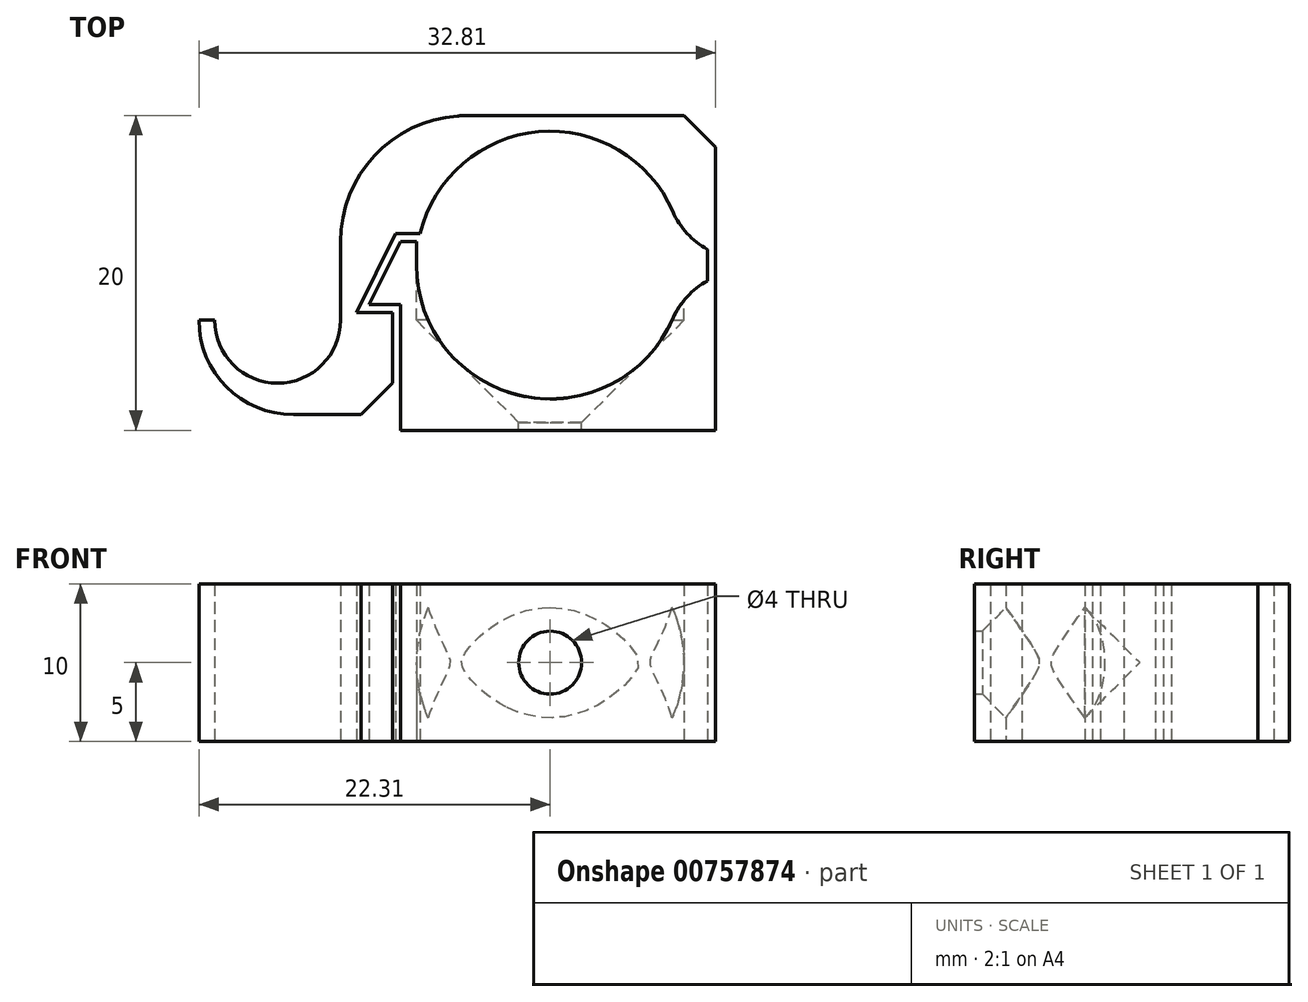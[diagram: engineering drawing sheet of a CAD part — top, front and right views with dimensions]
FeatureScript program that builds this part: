
annotation { "Feature Type Name" : "Feature", "Feature Type Description" : "" }
export const myFeature = defineFeature(function(context is Context, id is Id, definition is map)
    precondition{}
    {
        {
            var Q0;
            Q0=qCreatedBy(makeId("Top.planeOp"),FACE);
            var sketch = newSketch(context, id + "F0", { "sketchPlane" : qUnion([Q0])});
            skArc(sketch, "E0", {"start": v(-8.5, 0) * mm, "mid": v(8.44, -1) * mm, "end": v(-8.26, 2) * mm});
            skLineSegment(sketch, "E1", {"start": v(-9.5, 1.5) * mm, "end": v(-11.5, -2.5) * mm});
            skLineSegment(sketch, "E2", {"start": v(-11.5, -2.5) * mm, "end": v(-9.5, -2.5) * mm});
            skLineSegment(sketch, "E3", {"start": v(-9.5, -2.5) * mm, "end": v(-9.5, -10.5) * mm});
            skLineSegment(sketch, "E4", {"start": v(-9.5, -10.5) * mm, "end": v(10.5, -10.5) * mm});
            skLineSegment(sketch, "E5", {"start": v(10.5, -10.5) * mm, "end": v(10.5, 10.5) * mm});
            skCircle(sketch, "E6.0", {"center": v(0, 0) * mm, "radius": 10.5 * mm, "construction": true});
            skLineSegment(sketch, "E7", {"start": v(10.5, 10.5) * mm, "end": v(-13.3, 10.5) * mm});
            skLineSegment(sketch, "E8", {"start": v(-9.5, 1.5) * mm, "end": v(-8.5, 1.5) * mm});
            skLineSegment(sketch, "E9", {"start": v(-13.3, 10.5) * mm, "end": v(-13.3, -3.5) * mm});
            skLineSegment(sketch, "E10", {"start": v(-8.5, 1.5) * mm, "end": v(-8.5, 0) * mm});
            skLineSegment(sketch, "E11.0", {"start": v(-9.8, 2) * mm, "end": v(-8.26, 2) * mm});
            skLineSegment(sketch, "E11.1", {"start": v(-9.8, 2) * mm, "end": v(-12.3, -3) * mm});
            skLineSegment(sketch, "E12.0", {"start": v(-12.3, -3) * mm, "end": v(-10, -3) * mm});
            skLineSegment(sketch, "E13", {"start": v(-10, -3) * mm, "end": v(-10, -9.5) * mm});
            skLineSegment(sketch, "E14", {"start": v(-10, -9.5) * mm, "end": v(-13.3, -9.5) * mm});
            skLineSegment(sketch, "E15", {"start": v(-13.3, -9.5) * mm, "end": v(-22.3, -9.5) * mm});
            skLineSegment(sketch, "E16", {"start": v(-22.3, -9.5) * mm, "end": v(-22.3, -3.5) * mm});
            skLineSegment(sketch, "E17", {"start": v(-22.3, -3.5) * mm, "end": v(-21.3, -3.5) * mm});
            skArc(sketch, "E18", {"start": v(-21.3, -3.5) * mm, "mid": v(-17.3, -7.5) * mm, "end": v(-13.3, -3.5) * mm});
            skPoint(sketch, "E19", {"position": v(-17.3, -7.5) * mm});
            skPoint(sketch, "E20", {"position": v(8.5, 0) * mm});
            skLineSegment(sketch, "E21.bottom", {"start": v(7, 1) * mm, "end": v(10, 1) * mm});
            skLineSegment(sketch, "E21.top", {"start": v(7, -1) * mm, "end": v(10, -1) * mm});
            skLineSegment(sketch, "E21.left", {"start": v(7, 1) * mm, "end": v(7, -1) * mm});
            skLineSegment(sketch, "E21.right", {"start": v(10, 1) * mm, "end": v(10, -1) * mm});
            skLineSegment(sketch, "E22", {"start": v(-13.3, 9.5) * mm, "end": v(10.5, 9.5) * mm});
            skPoint(sketch, "E23", {"position": v(0, 8.5) * mm});
            skSolve(sketch);
        }
        {
            var Q0;
            Q0=makeQuery(id+"F0.imprint","IMPRINT",FACE,{"disambiguationData":[TD([[makeQuery(id+"F0.imprint","IMPRINT",EDGE,{"derivedFrom":sQuery(id+"F0.wireOp",EDGE,"E1")}),1.0]])]});
            extrude(context, id + "F1", {"entities" : qUnion([Q0]), "endBound" : BoundingType.SYMMETRIC, "depth" : 10 * mm, "offsetDistance" : 25 * mm});
        }
        {
            var Q0;
            Q0=qCreatedBy(makeId("Top.planeOp"),FACE);
            var sketch = newSketch(context, id + "F2", { "sketchPlane" : qUnion([Q0])});
            skLineSegment(sketch, "E24", {"start": v(0, 0) * mm, "end": v(0, -10.5) * mm, "construction": true});
            skPoint(sketch, "E25", {"position": v(-8.5, 1.5) * mm});
            skLineSegment(sketch, "E26", {"start": v(-8.5, 1.5) * mm, "end": v(-8.5, -3.5) * mm});
            skLineSegment(sketch, "E27", {"start": v(-8.5, -3.5) * mm, "end": v(-2, -10) * mm});
            skLineSegment(sketch, "E28", {"start": v(-2, -10) * mm, "end": v(-2, -10.5) * mm});
            skLineSegment(sketch, "E29", {"start": v(-2, -10.5) * mm, "end": v(0, -10.5) * mm});
            skLineSegment(sketch, "E30", {"start": v(-8.5, 1.5) * mm, "end": v(0, 1.5) * mm});
            skLineSegment(sketch, "E31", {"start": v(0, 1.5) * mm, "end": v(0, -10.5) * mm});
            skLineSegment(sketch, "E32", {"start": v(0.13, 0) * mm, "end": v(-8.5, 0) * mm});
            skSolve(sketch);
        }
        {
            var Q0;
            {var subQ1=sQuery(id+"F2.wireOp",EDGE,"E27");Q0=makeQuery(id+"F2.imprint","IMPRINT",FACE,{"disambiguationData":[TD([[makeQuery(id+"F2.imprint","IMPRINT",EDGE,{"derivedFrom":subQ1}),1.0]])]});}
            var Q1;
            Q1=sQuery(id+"F2.wireOp",EDGE,"E31");
            revolve(context, id + "F3", {"operationType" : NewBodyOperationType.REMOVE, "surfaceOperationType" : NewSurfaceOperationType.NEW, "entities" : qUnion([Q0]), "axis" : qUnion([Q1]), "revolveType" : RevolveType.FULL});
        }
        {
            var Q0;
            Q0=makeQuery(id+"F1.opExtrude","SWEPT_EDGE",EDGE,{"disambiguationData":[OSD([sQuery(id+"F0.wireOp",EDGE,"E13"),sQuery(id+"F0.wireOp",EDGE,"E14")])]});
            chamfer(context, id + "F4", {"entities" : qUnion([Q0]), "width" : 2 * mm, "tangentPropagation" : true});
        }
        {
            var Q0;
            Q0=makeQuery(id+"F1.opExtrude","SWEPT_EDGE",EDGE,{"disambiguationData":[OSD([sQuery(id+"F0.wireOp",EDGE,"E15"),sQuery(id+"F0.wireOp",EDGE,"E16")])]});
            fillet(context, id + "F5", {"entities" : qUnion([Q0]), "radius" : 6 * mm, "tangentPropagation" : true, "allowEdgeOverflow" : false});
        }
        {
            var Q0;
            Q0=makeQuery(id+"F1.opExtrude","SWEPT_EDGE",EDGE,{"disambiguationData":[OSD([sQuery(id+"F0.wireOp",EDGE,"E7"),sQuery(id+"F0.wireOp",EDGE,"E9")])]});
            chamfer(context, id + "F6", {"entities" : qUnion([Q0]), "width" : 4 * mm, "tangentPropagation" : true});
        }
        {
            var Q0;
            {var subQ0=sQuery(id+"F0.wireOp",EDGE,"E22");Q0=makeQuery(id+"F6.opChamfer","BLEND_EDGE",EDGE,{"blendedFrom":[makeQuery(id+"F1.opExtrude","SWEPT_EDGE",EDGE,{"disambiguationData":[OSD([sQuery(id+"F0.wireOp",EDGE,"E9"),subQ0])]}),makeQuery(id+"F1.opExtrude","SWEPT_FACE",FACE,{"disambiguationData":[OSD([subQ0])]})],"blendedInto":[makeQuery(id+"F1.opExtrude","SWEPT_FACE",FACE,{"disambiguationData":[OSD([subQ0])]})]});}
            fillet(context, id + "F7", {"entities" : qUnion([Q0]), "radius" : 10 * mm, "tangentPropagation" : true, "allowEdgeOverflow" : false});
        }
        {
            var Q0;
            {var subQ0=sQuery(id+"F0.wireOp",EDGE,"E9");Q0=makeQuery(id+"F6.opChamfer","BLEND_EDGE",EDGE,{"blendedFrom":[makeQuery(id+"F1.opExtrude","SWEPT_EDGE",EDGE,{"disambiguationData":[OSD([subQ0,sQuery(id+"F0.wireOp",EDGE,"E22")])]}),makeQuery(id+"F1.opExtrude","SWEPT_FACE",FACE,{"disambiguationData":[OSD([subQ0])]})],"blendedInto":[makeQuery(id+"F1.opExtrude","SWEPT_FACE",FACE,{"disambiguationData":[OSD([subQ0])]})]});}
            fillet(context, id + "F8", {"entities" : qUnion([Q0]), "radius" : 8 * mm, "tangentPropagation" : true, "allowEdgeOverflow" : false});
        }
        {
            var Q0;
            Q0=makeQuery(id+"F1.opExtrude","SWEPT_EDGE",EDGE,{"disambiguationData":[OSD([sQuery(id+"F0.wireOp",EDGE,"E0"),sQuery(id+"F0.wireOp",EDGE,"E21.bottom")])]});
            var Q1;
            {var subQ0=sQuery(id+"F0.wireOp",EDGE,"E10");var subQ1=sQuery(id+"F0.wireOp",EDGE,"E0");var subQ2=sQuery(id+"F0.wireOp",EDGE,"E21.top");Q1=makeQuery(id+"F3.boolean.opBoolean","SPLIT",EDGE,{"disambiguationData":[TD([makeQuery(id+"F1.opExtrude","CAP_FACE",FACE,{"disambiguationData":[OSD([subQ1,sQuery(id+"F0.wireOp",EDGE,"E1"),sQuery(id+"F0.wireOp",EDGE,"E2"),sQuery(id+"F0.wireOp",EDGE,"E3"),sQuery(id+"F0.wireOp",EDGE,"E4"),sQuery(id+"F0.wireOp",EDGE,"E5"),sQuery(id+"F0.wireOp",EDGE,"E8"),sQuery(id+"F0.wireOp",EDGE,"E9"),subQ0,sQuery(id+"F0.wireOp",EDGE,"E11.0"),sQuery(id+"F0.wireOp",EDGE,"E11.1"),sQuery(id+"F0.wireOp",EDGE,"E12.0"),sQuery(id+"F0.wireOp",EDGE,"E13"),sQuery(id+"F0.wireOp",EDGE,"E14"),sQuery(id+"F0.wireOp",EDGE,"E15"),sQuery(id+"F0.wireOp",EDGE,"E16"),sQuery(id+"F0.wireOp",EDGE,"E17"),sQuery(id+"F0.wireOp",EDGE,"E18"),sQuery(id+"F0.wireOp",EDGE,"E21.bottom"),subQ2,sQuery(id+"F0.wireOp",EDGE,"E21.right"),sQuery(id+"F0.wireOp",EDGE,"E22")])],"isStart":true})])],"derivedFrom":makeQuery(id+"F1.opExtrude","SWEPT_EDGE",EDGE,{"disambiguationData":[OSD([subQ1,subQ2])]})});}
            var Q2;
            {var subQ0=sQuery(id+"F0.wireOp",EDGE,"E10");var subQ1=sQuery(id+"F0.wireOp",EDGE,"E0");var subQ2=sQuery(id+"F0.wireOp",EDGE,"E21.top");Q2=makeQuery(id+"F3.boolean.opBoolean","SPLIT",EDGE,{"disambiguationData":[TD([makeQuery(id+"F1.opExtrude","CAP_FACE",FACE,{"disambiguationData":[OSD([subQ1,sQuery(id+"F0.wireOp",EDGE,"E1"),sQuery(id+"F0.wireOp",EDGE,"E2"),sQuery(id+"F0.wireOp",EDGE,"E3"),sQuery(id+"F0.wireOp",EDGE,"E4"),sQuery(id+"F0.wireOp",EDGE,"E5"),sQuery(id+"F0.wireOp",EDGE,"E8"),sQuery(id+"F0.wireOp",EDGE,"E9"),subQ0,sQuery(id+"F0.wireOp",EDGE,"E11.0"),sQuery(id+"F0.wireOp",EDGE,"E11.1"),sQuery(id+"F0.wireOp",EDGE,"E12.0"),sQuery(id+"F0.wireOp",EDGE,"E13"),sQuery(id+"F0.wireOp",EDGE,"E14"),sQuery(id+"F0.wireOp",EDGE,"E15"),sQuery(id+"F0.wireOp",EDGE,"E16"),sQuery(id+"F0.wireOp",EDGE,"E17"),sQuery(id+"F0.wireOp",EDGE,"E18"),sQuery(id+"F0.wireOp",EDGE,"E21.bottom"),subQ2,sQuery(id+"F0.wireOp",EDGE,"E21.right"),sQuery(id+"F0.wireOp",EDGE,"E22")])],"isStart":false})])],"derivedFrom":makeQuery(id+"F1.opExtrude","SWEPT_EDGE",EDGE,{"disambiguationData":[OSD([subQ1,subQ2])]})});}
            fillet(context, id + "F9", {"entities" : qUnion([Q0, Q1, Q2]), "radius" : 5 * mm, "tangentPropagation" : true, "allowEdgeOverflow" : false});
        }
        {
            var Q0;
            Q0=makeQuery(id+"F1.opExtrude","SWEPT_EDGE",EDGE,{"disambiguationData":[OSD([sQuery(id+"F0.wireOp",EDGE,"E5"),sQuery(id+"F0.wireOp",EDGE,"E22")])]});
            chamfer(context, id + "F10", {"entities" : qUnion([Q0]), "width" : 2 * mm, "tangentPropagation" : true});
        }
    });
